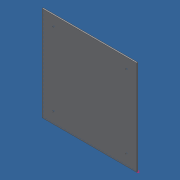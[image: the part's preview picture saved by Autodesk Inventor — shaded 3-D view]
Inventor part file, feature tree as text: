
AUTODESK INVENTOR PART (.ipt)
format: ipt  version: 2021 (Build 250183000, 183)  size: 90,624 bytes
history: native  units: mm
features: sketch x2, extrude x1
ambient origin geometry x8: Origin, YZ Plane, XZ Plane, XY Plane, X Axis, Y Axis, Z Axis, Center Point
bodies: Solid1 (feature_tree)
feature tree (3):
  extrude  "Extrusion1"  Depth=310.0mm
  sketch  "Sketch2"  dims[d2=240.0mm d3=240.0mm d4=240.0mm d5=240.0mm d6=35.0mm d7=35.0mm d8=3.5mm d9=3.5mm d10=3.5mm d11=3.5mm d12=4.0mm d13=0.0mm]
  sketch  "Sketch1"  dims[d0=310.0mm d1=310.0mm]
